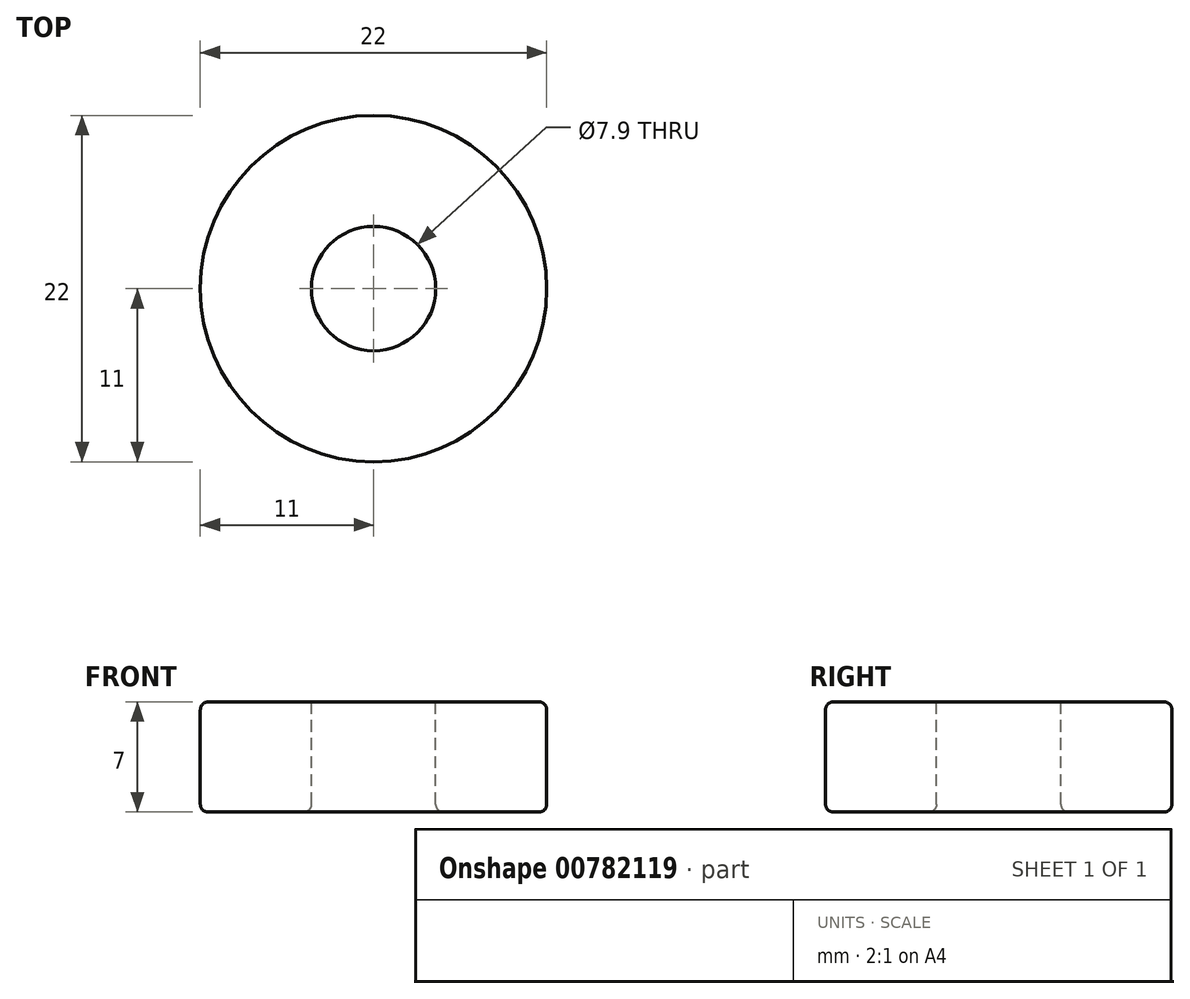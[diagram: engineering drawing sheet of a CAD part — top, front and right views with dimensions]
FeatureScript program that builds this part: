
annotation { "Feature Type Name" : "Feature", "Feature Type Description" : "" }
export const myFeature = defineFeature(function(context is Context, id is Id, definition is map)
    precondition{}
    {
        {
            var Q0;
            Q0=qCreatedBy(makeId("Top.planeOp"),FACE);
            var sketch = newSketch(context, id + "F0", { "sketchPlane" : qUnion([Q0])});
            skCircle(sketch, "E0", {"center": v(0, 0) * mm, "radius": 11 * mm});
            skSolve(sketch);
        }
        {
            var Q0;
            Q0 = qSketchRegion(id + "F0", true);
            extrude(context, id + "F1", {"entities" : qUnion([Q0]), "depth" : 7 * mm, "offsetDistance" : 25 * mm});
        }
        {
            var Q0;
            Q0=makeQuery(id+"F1.opExtrude","CAP_FACE",FACE,{"disambiguationData":[OSD([sQuery(id+"F0.wireOp",EDGE,"E0")])],"isStart":false});
            var sketch = newSketch(context, id + "F2", { "sketchPlane" : qUnion([Q0])});
            skCircle(sketch, "E1", {"center": v(0, 0) * mm, "radius": 3.95 * mm});
            skSolve(sketch);
        }
        {
            var Q0;
            Q0 = qSketchRegion(id + "F2", true);
            extrude(context, id + "F3", {"entities" : qUnion([Q0]), "operationType" : NewBodyOperationType.REMOVE, "endBound" : BoundingType.THROUGH_ALL, "oppositeDirection" : true, "depth" : 25 * mm, "offsetDistance" : 25 * mm});
        }
        {
            var Q0;
            Q0=makeQuery(id+"F1.opExtrude","CAP_EDGE",EDGE,{"disambiguationData":[OSD([sQuery(id+"F0.wireOp",EDGE,"E0")])],"isStart":false});
            var Q1;
            Q1=makeQuery(id+"F3.boolean.opBoolean","COPY",EDGE,{"derivedFrom":makeQuery(id+"F3.opExtrude","CAP_EDGE",EDGE,{"disambiguationData":[OSD([sQuery(id+"F2.wireOp",EDGE,"E1")])],"isStart":true})});
            var Q2;
            Q2=makeQuery(id+"F1.opExtrude","CAP_EDGE",EDGE,{"disambiguationData":[OSD([sQuery(id+"F0.wireOp",EDGE,"E0")])],"isStart":true});
            var Q3;
            Q3=makeQuery(id+"F3.boolean.opBoolean","INTERSECT",EDGE,{"derivedFrom":[makeQuery(id+"F1.opExtrude","CAP_FACE",FACE,{"disambiguationData":[OSD([sQuery(id+"F0.wireOp",EDGE,"E0")])],"isStart":true}),makeQuery(id+"F3.opExtrude","SWEPT_FACE",FACE,{"disambiguationData":[OSD([sQuery(id+"F2.wireOp",EDGE,"E1")])]})]});
            fillet(context, id + "F4", {"entities" : qUnion([Q0, Q1, Q2, Q3]), "radius" : .5 * mm, "tangentPropagation" : true, "allowEdgeOverflow" : false});
        }
    });
